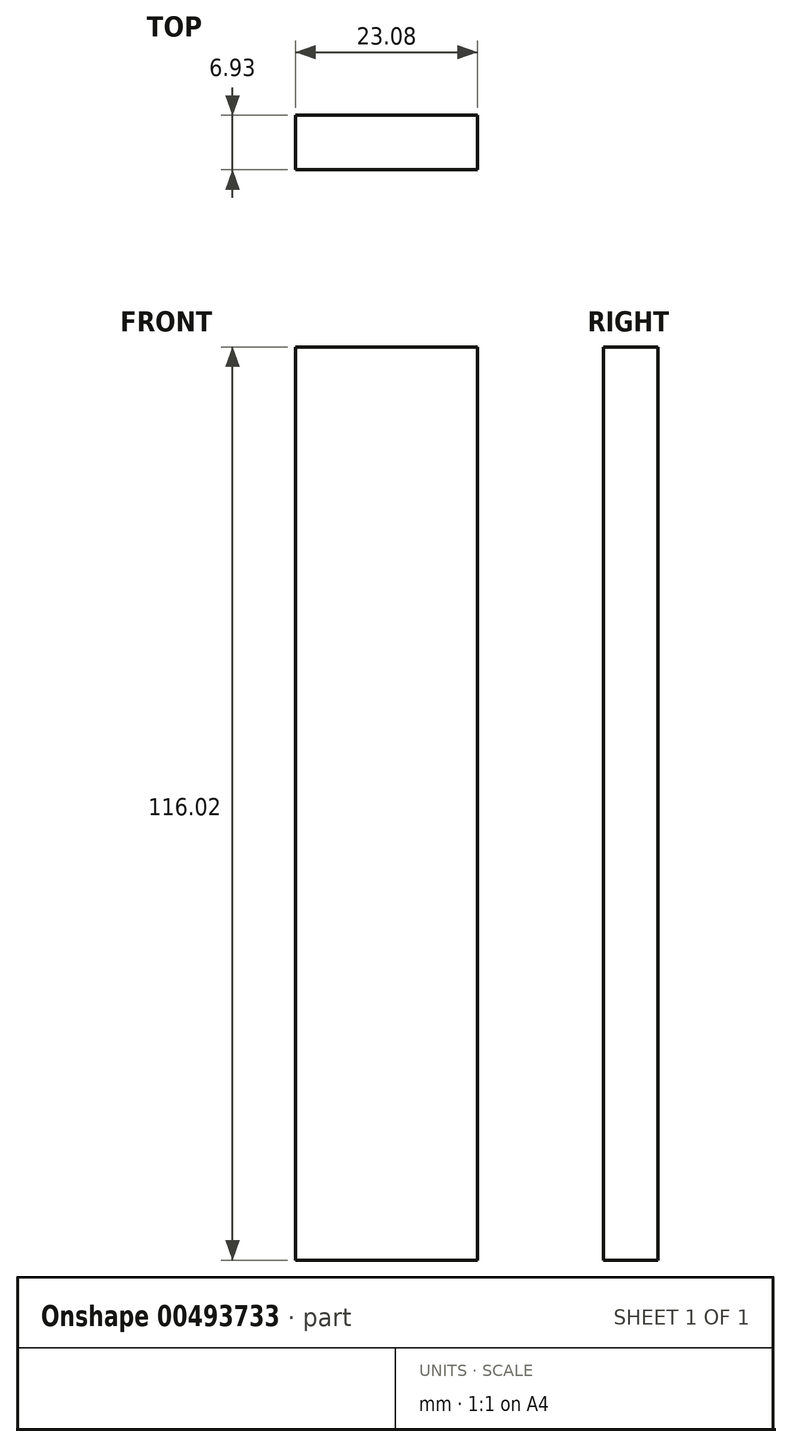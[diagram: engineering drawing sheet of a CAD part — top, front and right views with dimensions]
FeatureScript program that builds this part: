
annotation { "Feature Type Name" : "Feature", "Feature Type Description" : "" }
export const myFeature = defineFeature(function(context is Context, id is Id, definition is map)
    precondition{}
    {
        {
            var Q0;
            Q0=qCreatedBy(makeId("Front.planeOp"),FACE);
            var sketch = newSketch(context, id + "F0", { "sketchPlane" : qUnion([Q0])});
            skLineSegment(sketch, "E0.bottom", {"start": v(11.54, -58) * mm, "end": v(-11.54, -58) * mm});
            skLineSegment(sketch, "E0.top", {"start": v(11.54, 58.01) * mm, "end": v(-11.54, 58.01) * mm});
            skLineSegment(sketch, "E0.left", {"start": v(11.54, -58) * mm, "end": v(11.54, 58.01) * mm});
            skLineSegment(sketch, "E0.right", {"start": v(-11.54, -58) * mm, "end": v(-11.54, 58.01) * mm});
            skPoint(sketch, "E0.middle", {"position": v(0, 0) * mm});
            skSolve(sketch);
        }
        {
            var Q0;
            Q0=makeQuery(id+"F0.imprint","IMPRINT",FACE,{"disambiguationData":[TD([[makeQuery(id+"F0.imprint","IMPRINT",EDGE,{"derivedFrom":sQuery(id+"F0.wireOp",EDGE,"E0.bottom")}),-1.0]])]});
            extrude(context, id + "F1", {"entities" : qUnion([Q0]), "depth" : 6.93 * mm});
        }
    });
